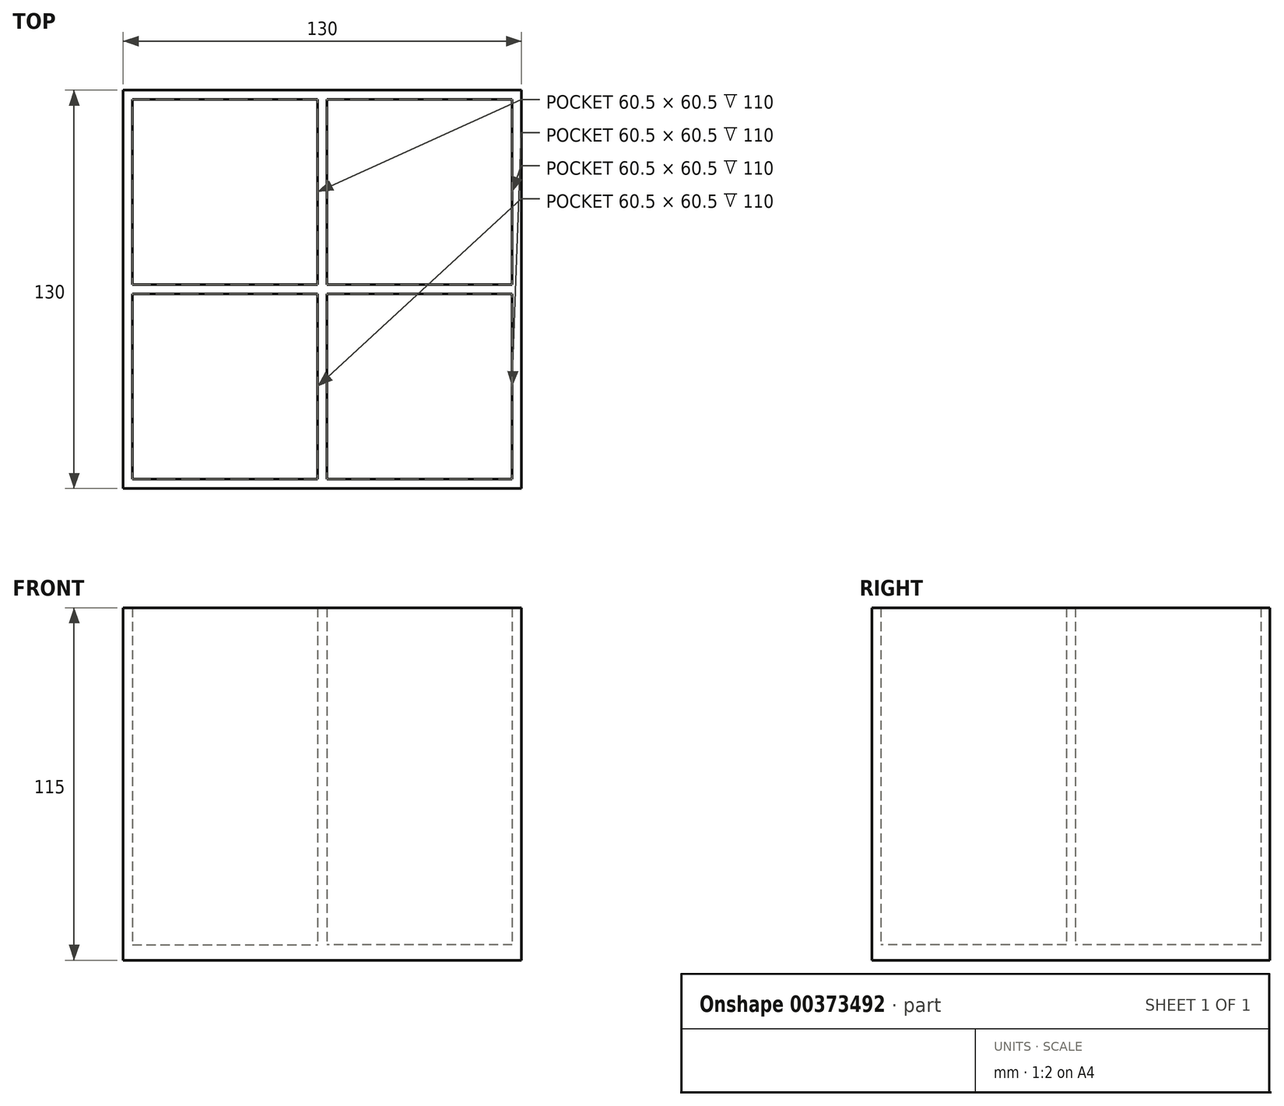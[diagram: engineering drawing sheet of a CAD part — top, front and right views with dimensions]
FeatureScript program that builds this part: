
annotation { "Feature Type Name" : "Feature", "Feature Type Description" : "" }
export const myFeature = defineFeature(function(context is Context, id is Id, definition is map)
    precondition{}
    {
        {
            var Q0;
            Q0=qCreatedBy(makeId("Top.planeOp"),FACE);
            var sketch = newSketch(context, id + "F0", { "sketchPlane" : qUnion([Q0])});
            skLineSegment(sketch, "E0.bottom", {"start": v(-65, 65) * mm, "end": v(65, 65) * mm});
            skLineSegment(sketch, "E0.top", {"start": v(-65, -65) * mm, "end": v(65, -65) * mm});
            skLineSegment(sketch, "E0.left", {"start": v(-65, 65) * mm, "end": v(-65, -65) * mm});
            skLineSegment(sketch, "E0.right", {"start": v(65, 65) * mm, "end": v(65, -65) * mm});
            skLineSegment(sketch, "E1", {"start": v(65, 65) * mm, "end": v(-65, -65) * mm, "construction": true});
            skLineSegment(sketch, "E2.bottom", {"start": v(-62, 62) * mm, "end": v(62, 62) * mm});
            skLineSegment(sketch, "E2.top", {"start": v(-62, -62) * mm, "end": v(62, -62) * mm});
            skLineSegment(sketch, "E2.left", {"start": v(-62, 62) * mm, "end": v(-62, -62) * mm});
            skLineSegment(sketch, "E2.right", {"start": v(62, 62) * mm, "end": v(62, -62) * mm});
            skLineSegment(sketch, "E3", {"start": v(62, -62) * mm, "end": v(62, -65) * mm, "construction": true});
            skLineSegment(sketch, "E4", {"start": v(62, -62) * mm, "end": v(65, -62) * mm, "construction": true});
            skLineSegment(sketch, "E5", {"start": v(-62, 62) * mm, "end": v(-62, 65) * mm, "construction": true});
            skLineSegment(sketch, "E6", {"start": v(-62, 62) * mm, "end": v(-65, 62) * mm, "construction": true});
            skLineSegment(sketch, "E7", {"start": v(-62, 1.5) * mm, "end": v(62, 1.5) * mm});
            skLineSegment(sketch, "E8", {"start": v(62, -1.5) * mm, "end": v(-62, -1.5) * mm});
            skLineSegment(sketch, "E9", {"start": v(-1.5, 62) * mm, "end": v(-1.5, -62) * mm});
            skLineSegment(sketch, "E10", {"start": v(1.5, -62) * mm, "end": v(1.5, 62) * mm});
            skSolve(sketch);
        }
        {
            var Q0;
            Q0=makeQuery(id+"F0.imprint","IMPRINT",FACE,{"disambiguationData":[TD([[makeQuery(id+"F0.imprint","IMPRINT",EDGE,{"derivedFrom":sQuery(id+"F0.wireOp",EDGE,"E0.bottom")}),-1.0]])]});
            var Q1;
            {var subQ0=sQuery(id+"F0.wireOp",EDGE,"E7");Q1=makeQuery(id+"F0.imprint","IMPRINT",FACE,{"disambiguationData":[TD([[makeQuery(id+"F0.imprint","IMPRINT",EDGE,{"derivedFrom":subQ0}),-1.0]])]});}
            var Q2;
            {var subQ0=sQuery(id+"F0.wireOp",EDGE,"E9");var subQ1=sQuery(id+"F0.wireOp",EDGE,"E2.bottom");var subQ2=makeQuery(id+"F0.imprint","INTERSECT",VERTEX,{"derivedFrom":[subQ1,subQ0]});Q2=makeQuery(id+"F0.imprint","IMPRINT",FACE,{"disambiguationData":[TD([[makeQuery(id+"F0.imprint","IMPRINT",EDGE,{"disambiguationData":[TD([[subQ2,-1.0]])],"derivedFrom":subQ1}),-1.0]])]});}
            var Q3;
            {var subQ0=sQuery(id+"F0.wireOp",EDGE,"E9");var subQ1=sQuery(id+"F0.wireOp",EDGE,"E2.top");var subQ2=makeQuery(id+"F0.imprint","INTERSECT",VERTEX,{"derivedFrom":[subQ1,subQ0]});Q3=makeQuery(id+"F0.imprint","IMPRINT",FACE,{"disambiguationData":[TD([[makeQuery(id+"F0.imprint","IMPRINT",EDGE,{"disambiguationData":[TD([[subQ2,-1.0]])],"derivedFrom":subQ1}),1.0]])]});}
            extrude(context, id + "F1", {"entities" : qUnion([Q0, Q1, Q2, Q3]), "depth" : 110 * mm});
        }
        {
            var Q0;
            {var subQ0=sQuery(id+"F0.wireOp",EDGE,"E2.bottom");Q0=makeQuery(id+"F0.imprint","IMPRINT",FACE,{"disambiguationData":[TD([[makeQuery(id+"F0.imprint","IMPRINT",EDGE,{"derivedFrom":subQ0}),-1.0]])]});}
            var Q1;
            {var subQ0=sQuery(id+"F0.wireOp",EDGE,"E2.top");Q1=makeQuery(id+"F0.imprint","IMPRINT",FACE,{"disambiguationData":[TD([[makeQuery(id+"F0.imprint","IMPRINT",EDGE,{"derivedFrom":subQ0}),1.0]])]});}
            var Q2;
            Q2=makeQuery(id+"F0.imprint","IMPRINT",FACE,{"disambiguationData":[TD([[makeQuery(id+"F0.imprint","IMPRINT",EDGE,{"derivedFrom":sQuery(id+"F0.wireOp",EDGE,"E0.bottom")}),-1.0]])]});
            var Q3;
            {var subQ0=sQuery(id+"F0.wireOp",EDGE,"E7");Q3=makeQuery(id+"F0.imprint","IMPRINT",FACE,{"disambiguationData":[TD([[makeQuery(id+"F0.imprint","IMPRINT",EDGE,{"derivedFrom":subQ0}),-1.0]])]});}
            extrude(context, id + "F2", {"entities" : qUnion([Q0, Q1, Q2, Q3]), "operationType" : NewBodyOperationType.ADD, "oppositeDirection" : true, "depth" : 5 * mm});
        }
    });
